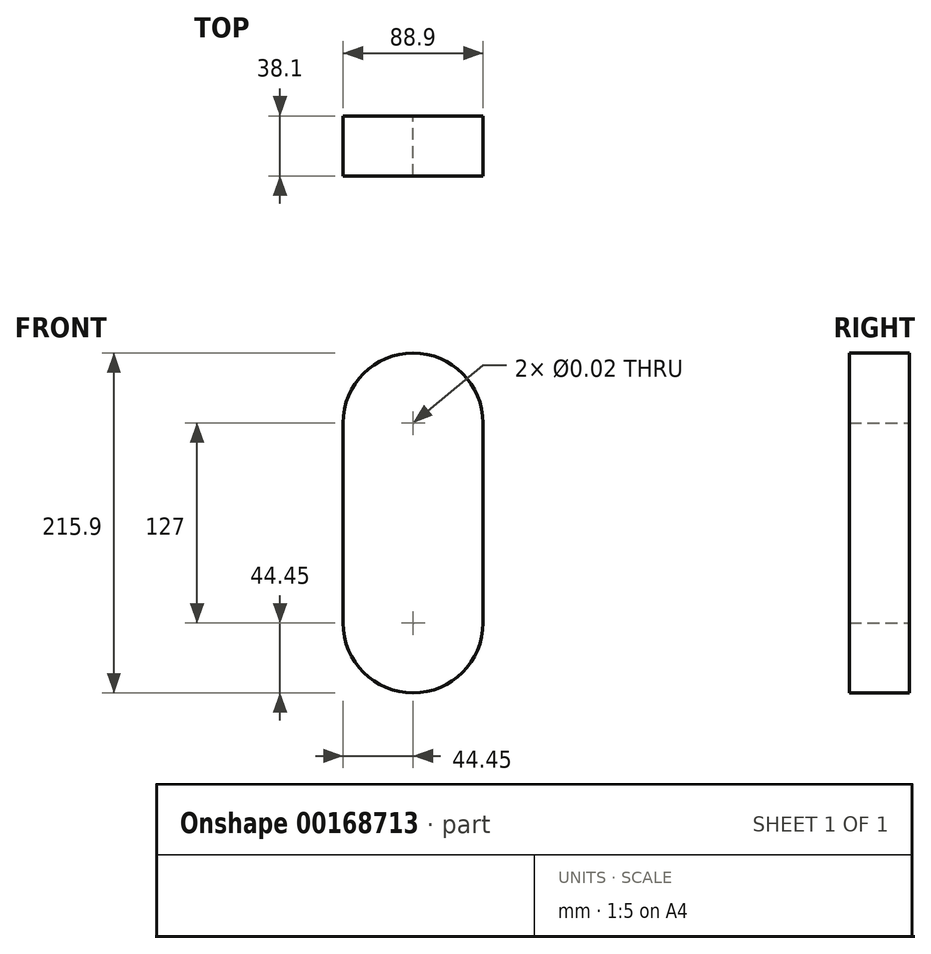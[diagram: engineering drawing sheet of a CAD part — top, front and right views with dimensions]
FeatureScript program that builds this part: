
annotation { "Feature Type Name" : "Feature", "Feature Type Description" : "" }
export const myFeature = defineFeature(function(context is Context, id is Id, definition is map)
    precondition{}
    {
        {
            var Q0;
            Q0=qCreatedBy(makeId("Front.planeOp"),FACE);
            var sketch = newSketch(context, id + "F0", { "sketchPlane" : qUnion([Q0])});
            skLineSegment(sketch, "E0.left", {"start": v(44.45, 63.5) * mm, "end": v(44.45, -63.5) * mm});
            skLineSegment(sketch, "E0.right", {"start": v(-44.45, 63.5) * mm, "end": v(-44.45, -63.5) * mm});
            skPoint(sketch, "E0.middle", {"position": v(0, 0) * mm});
            skArc(sketch, "E1", {"start": v(44.45, 63.5) * mm, "mid": v(0, 107.95) * mm, "end": v(-44.45, 63.5) * mm});
            skArc(sketch, "E2", {"start": v(-44.45, -63.5) * mm, "mid": v(0, -107.95) * mm, "end": v(44.45, -63.5) * mm});
            skLineSegment(sketch, "E3", {"start": v(-44.45, 63.5) * mm, "end": v(44.45, 63.5) * mm, "construction": true});
            skSolve(sketch);
        }
        {
            var Q0;
            Q0=qSketchRegion(id+"F0",true);
            extrude(context, id + "F1", {"entities" : qUnion([Q0]), "depth" : 38.1 * mm});
        }
        {
            var Q0;
            Q0=sQuery(id+"F0.wireOp",VERTEX,"E1.center");
            var Q1;
            Q1=sQuery(id+"F0.wireOp",VERTEX,"E2.center");
            var Q2;
            Q2=makeQuery(id+"F1.opExtrude","SWEPT_BODY",BODY,{"disambiguationData":[OSD([sQuery(id+"F0.wireOp",EDGE,"E0.left"),sQuery(id+"F0.wireOp",EDGE,"E0.right"),sQuery(id+"F0.wireOp",EDGE,"E1"),sQuery(id+"F0.wireOp",EDGE,"E2")])]});
            hole(context, id + "F2", {"style" : HoleStyle.SIMPLE, "endStyle" : HoleEndStyle.THROUGH, "oppositeDirection" : true, "standardTappedOrClearance" : lookupTablePath({ "standard" : "ANSI", "size" : "1/2 (0.5)", "type" : "Drilled" }), "standardBlindInLast" : lookupTablePath({ "standard" : "ANSI", "size" : "1/2", "type" : "Drilled" }), "holeDiameter" : 1 / 50.8 * mm, "locations" : qUnion([Q0, Q1]), "scope" : qUnion([Q2]), "isTappedThrough" : true});
        }
    });
